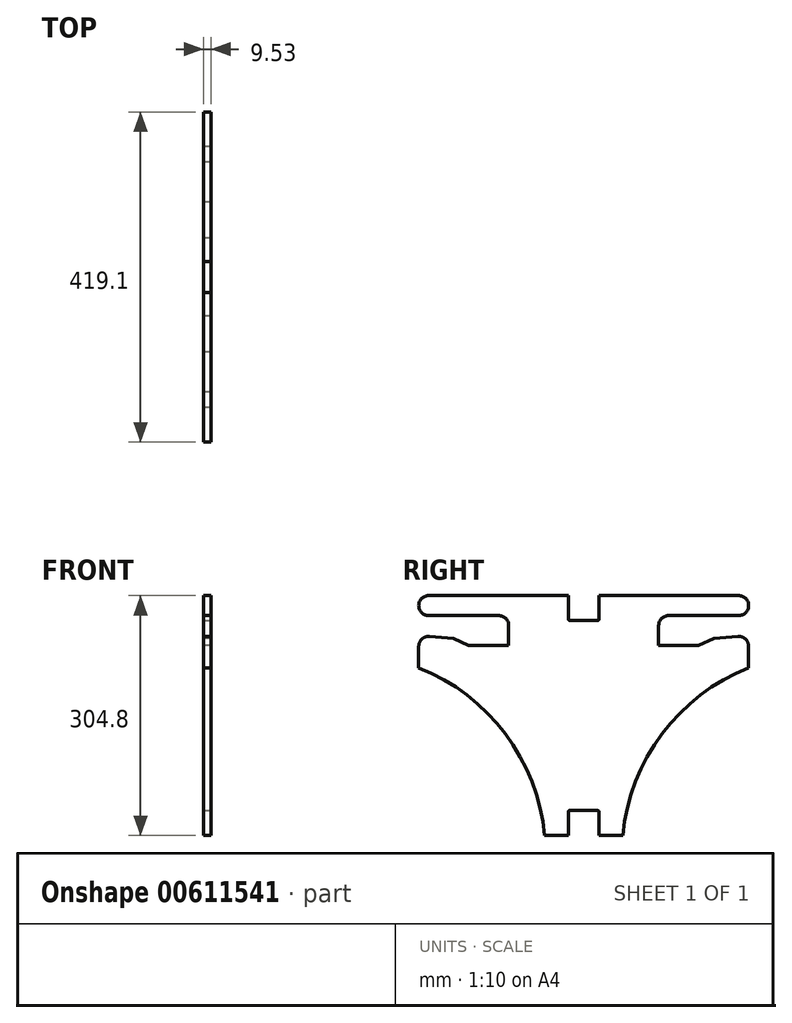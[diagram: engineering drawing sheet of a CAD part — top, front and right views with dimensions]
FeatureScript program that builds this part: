
annotation { "Feature Type Name" : "Feature", "Feature Type Description" : "" }
export const myFeature = defineFeature(function(context is Context, id is Id, definition is map)
    precondition{}
    {
        {
            var Q0;
            Q0=qCreatedBy(makeId("Right.planeOp"),FACE);
            var sketch = newSketch(context, id + "F0", { "sketchPlane" : qUnion([Q0])});
            skLineSegment(sketch, "E0.top", {"start": v(0, -31.75) * mm, "end": v(29.85, -31.75) * mm});
            skLineSegment(sketch, "E0.right", {"start": v(31.75, 0) * mm, "end": v(31.75, -29.84) * mm});
            skLineSegment(sketch, "E1", {"start": v(31.75, 0) * mm, "end": v(209.55, 0) * mm});
            skLineSegment(sketch, "E2", {"start": v(222.25, -12.7) * mm, "end": v(222.25, -12.7) * mm});
            skLineSegment(sketch, "E3", {"start": v(209.55, -25.4) * mm, "end": v(120.65, -25.4) * mm});
            skLineSegment(sketch, "E4", {"start": v(107.95, -38.1) * mm, "end": v(107.95, -63.5) * mm});
            skLineSegment(sketch, "E5", {"start": v(107.95, -63.5) * mm, "end": v(158.75, -63.5) * mm});
            skLineSegment(sketch, "E6", {"start": v(222.25, -64.65) * mm, "end": v(222.25, -91.85) * mm});
            skLineSegment(sketch, "E7", {"start": v(208.45, -52) * mm, "end": v(178.38, -54.6) * mm});
            skLineSegment(sketch, "E8", {"start": v(178.38, -54.6) * mm, "end": v(158.75, -63.5) * mm});
            skPoint(sketch, "E9.visualSharp", {"position": v(222.25, -25.4) * mm});
            skArc(sketch, "E9.filletArc", {"start": v(209.55, -25.4) * mm, "mid": v(218.53, -21.68) * mm, "end": v(222.25, -12.7) * mm});
            skPoint(sketch, "E10.visualSharp", {"position": v(222.25, 0) * mm});
            skArc(sketch, "E10.filletArc", {"start": v(222.25, -12.7) * mm, "mid": v(218.53, -3.72) * mm, "end": v(209.55, 0) * mm});
            skPoint(sketch, "E11.visualSharp", {"position": v(107.95, -25.4) * mm});
            skArc(sketch, "E11.filletArc", {"start": v(120.65, -25.4) * mm, "mid": v(111.67, -29.12) * mm, "end": v(107.95, -38.1) * mm});
            skPoint(sketch, "E12.visualSharp", {"position": v(222.25, -50.8) * mm});
            skArc(sketch, "E12.filletArc", {"start": v(222.25, -64.65) * mm, "mid": v(218.13, -55.3) * mm, "end": v(208.45, -52) * mm});
            skLineSegment(sketch, "E13", {"start": v(0, -31.75) * mm, "end": v(0, -273.05) * mm});
            skLineSegment(sketch, "E14", {"start": v(0, -273.05) * mm, "end": v(29.85, -273.05) * mm});
            skLineSegment(sketch, "E15", {"start": v(31.75, -274.95) * mm, "end": v(31.75, -304.8) * mm});
            skLineSegment(sketch, "E16", {"start": v(31.75, -304.8) * mm, "end": v(62.46, -304.8) * mm});
            skArc(sketch, "E17", {"start": v(222.25, -91.85) * mm, "mid": v(112.22, -175.71) * mm, "end": v(62.46, -304.8) * mm});
            skPoint(sketch, "E18.visualSharp", {"position": v(31.75, -31.75) * mm});
            skArc(sketch, "E18.filletArc", {"start": v(29.85, -31.75) * mm, "mid": v(31.2, -31.2) * mm, "end": v(31.75, -29.84) * mm});
            skPoint(sketch, "E19.visualSharp", {"position": v(31.75, -273.05) * mm});
            skArc(sketch, "E19.filletArc", {"start": v(31.75, -274.95) * mm, "mid": v(31.2, -273.6) * mm, "end": v(29.85, -273.05) * mm});
            skSolve(sketch);
        }
        {
            var Q0;
            Q0 = qSketchRegion(id + "F0", true);
            extrude(context, id + "F1", {"entities" : qUnion([Q0]), "depth" : 9.52 * mm, "offsetDistance" : 25.4 * mm});
        }
        {
            var Q0;
            Q0=makeQuery(id+"F1.opExtrude","CAP_FACE",FACE,{"disambiguationData":[OSD([sQuery(id+"F0.wireOp",EDGE,"E0.top"),sQuery(id+"F0.wireOp",EDGE,"E0.right"),sQuery(id+"F0.wireOp",EDGE,"E1"),sQuery(id+"F0.wireOp",EDGE,"E3"),sQuery(id+"F0.wireOp",EDGE,"E4"),sQuery(id+"F0.wireOp",EDGE,"E5"),sQuery(id+"F0.wireOp",EDGE,"E6"),sQuery(id+"F0.wireOp",EDGE,"E7"),sQuery(id+"F0.wireOp",EDGE,"E8"),sQuery(id+"F0.wireOp",EDGE,"E9.filletArc"),sQuery(id+"F0.wireOp",EDGE,"E10.filletArc"),sQuery(id+"F0.wireOp",EDGE,"E11.filletArc"),sQuery(id+"F0.wireOp",EDGE,"E12.filletArc"),sQuery(id+"F0.wireOp",EDGE,"E13"),sQuery(id+"F0.wireOp",EDGE,"E14"),sQuery(id+"F0.wireOp",EDGE,"E15"),sQuery(id+"F0.wireOp",EDGE,"E16"),sQuery(id+"F0.wireOp",EDGE,"E17"),sQuery(id+"F0.wireOp",EDGE,"E18.filletArc"),sQuery(id+"F0.wireOp",EDGE,"E19.filletArc")])],"isStart":false});
            var sketch = newSketch(context, id + "F2", { "sketchPlane" : qUnion([Q0])});
            skLineSegment(sketch, "E20.bottom", {"start": v(0, -31.75) * mm, "end": v(12.7, -31.75) * mm});
            skLineSegment(sketch, "E20.top", {"start": v(0, -273.05) * mm, "end": v(12.7, -273.05) * mm});
            skLineSegment(sketch, "E20.left", {"start": v(0, -31.75) * mm, "end": v(0, -273.05) * mm});
            skLineSegment(sketch, "E20.right", {"start": v(12.7, -31.75) * mm, "end": v(12.7, -273.05) * mm});
            skSolve(sketch);
        }
        {
            var Q0;
            Q0 = qSketchRegion(id + "F2", true);
            extrude(context, id + "F3", {"entities" : qUnion([Q0]), "operationType" : NewBodyOperationType.REMOVE, "oppositeDirection" : true, "depth" : 25.4 * mm, "offsetDistance" : 25.4 * mm});
        }
        {
            var Q0;
            Q0=makeQuery(id+"F1.opExtrude","SWEPT_BODY",BODY,{"disambiguationData":[OSD([sQuery(id+"F0.wireOp",EDGE,"E0.top"),sQuery(id+"F0.wireOp",EDGE,"E0.right"),sQuery(id+"F0.wireOp",EDGE,"E1"),sQuery(id+"F0.wireOp",EDGE,"E3"),sQuery(id+"F0.wireOp",EDGE,"E4"),sQuery(id+"F0.wireOp",EDGE,"E5"),sQuery(id+"F0.wireOp",EDGE,"E6"),sQuery(id+"F0.wireOp",EDGE,"E7"),sQuery(id+"F0.wireOp",EDGE,"E8"),sQuery(id+"F0.wireOp",EDGE,"E9.filletArc"),sQuery(id+"F0.wireOp",EDGE,"E10.filletArc"),sQuery(id+"F0.wireOp",EDGE,"E11.filletArc"),sQuery(id+"F0.wireOp",EDGE,"E12.filletArc"),sQuery(id+"F0.wireOp",EDGE,"E13"),sQuery(id+"F0.wireOp",EDGE,"E14"),sQuery(id+"F0.wireOp",EDGE,"E15"),sQuery(id+"F0.wireOp",EDGE,"E16"),sQuery(id+"F0.wireOp",EDGE,"E17"),sQuery(id+"F0.wireOp",EDGE,"E18.filletArc"),sQuery(id+"F0.wireOp",EDGE,"E19.filletArc")])]});
            var Q1;
            Q1=makeQuery(id+"F3.boolean.opBoolean","COPY",FACE,{"derivedFrom":makeQuery(id+"F3.opExtrude","SWEPT_FACE",FACE,{"disambiguationData":[OSD([sQuery(id+"F2.wireOp",EDGE,"E20.right")])]})});
            mirror(context, id + "F4", {"operationType" : NewBodyOperationType.ADD, "entities" : qUnion([Q0]), "mirrorPlane" : qUnion([Q1])});
        }
        {
            var Q0;
            {var subQ0=makeQuery(id+"F1.opExtrude","CAP_FACE",FACE,{"disambiguationData":[OSD([sQuery(id+"F0.wireOp",EDGE,"E0.top"),sQuery(id+"F0.wireOp",EDGE,"E0.right"),sQuery(id+"F0.wireOp",EDGE,"E1"),sQuery(id+"F0.wireOp",EDGE,"E3"),sQuery(id+"F0.wireOp",EDGE,"E4"),sQuery(id+"F0.wireOp",EDGE,"E5"),sQuery(id+"F0.wireOp",EDGE,"E6"),sQuery(id+"F0.wireOp",EDGE,"E7"),sQuery(id+"F0.wireOp",EDGE,"E8"),sQuery(id+"F0.wireOp",EDGE,"E9.filletArc"),sQuery(id+"F0.wireOp",EDGE,"E10.filletArc"),sQuery(id+"F0.wireOp",EDGE,"E11.filletArc"),sQuery(id+"F0.wireOp",EDGE,"E12.filletArc"),sQuery(id+"F0.wireOp",EDGE,"E13"),sQuery(id+"F0.wireOp",EDGE,"E14"),sQuery(id+"F0.wireOp",EDGE,"E15"),sQuery(id+"F0.wireOp",EDGE,"E16"),sQuery(id+"F0.wireOp",EDGE,"E17"),sQuery(id+"F0.wireOp",EDGE,"E18.filletArc"),sQuery(id+"F0.wireOp",EDGE,"E19.filletArc")])],"isStart":false});Q0=makeQuery(id+"F4.boolean.opBoolean","MERGE",FACE,{"derivedFrom":[subQ0,makeQuery(id+"F4.opPattern","COPY",FACE,{"derivedFrom":subQ0,"instanceName":"1"})]});}
            var sketch = newSketch(context, id + "F5", { "sketchPlane" : qUnion([Q0])});
            skLineSegment(sketch, "E21.bottom", {"start": v(-6.75, 0) * mm, "end": v(32.15, 0) * mm});
            skLineSegment(sketch, "E21.top", {"start": v(-4.84, -31.75) * mm, "end": v(30.24, -31.75) * mm});
            skLineSegment(sketch, "E21.left", {"start": v(-6.75, 0) * mm, "end": v(-6.75, -29.85) * mm});
            skLineSegment(sketch, "E21.right", {"start": v(32.15, 0) * mm, "end": v(32.15, -29.84) * mm});
            skPoint(sketch, "E22.visualSharp", {"position": v(-6.75, -31.75) * mm});
            skArc(sketch, "E22.filletArc", {"start": v(-6.75, -29.85) * mm, "mid": v(-6.19, -31.2) * mm, "end": v(-4.84, -31.75) * mm});
            skPoint(sketch, "E23.visualSharp", {"position": v(32.15, -31.75) * mm});
            skArc(sketch, "E23.filletArc", {"start": v(30.24, -31.75) * mm, "mid": v(31.59, -31.2) * mm, "end": v(32.15, -29.84) * mm});
            skLineSegment(sketch, "E24.bottom", {"start": v(-6.75, -304.8) * mm, "end": v(32.15, -304.8) * mm});
            skLineSegment(sketch, "E24.top", {"start": v(-4.84, -273.05) * mm, "end": v(30.24, -273.05) * mm});
            skLineSegment(sketch, "E24.left", {"start": v(-6.75, -304.8) * mm, "end": v(-6.75, -274.95) * mm});
            skLineSegment(sketch, "E24.right", {"start": v(32.15, -304.8) * mm, "end": v(32.15, -274.95) * mm});
            skPoint(sketch, "E25.visualSharp", {"position": v(-6.75, -273.05) * mm});
            skArc(sketch, "E25.filletArc", {"start": v(-4.84, -273.05) * mm, "mid": v(-6.19, -273.6) * mm, "end": v(-6.75, -274.95) * mm});
            skPoint(sketch, "E26.visualSharp", {"position": v(32.15, -273.05) * mm});
            skArc(sketch, "E26.filletArc", {"start": v(32.15, -274.95) * mm, "mid": v(31.59, -273.6) * mm, "end": v(30.24, -273.05) * mm});
            skSolve(sketch);
        }
        {
            var Q0;
            Q0 = qSketchRegion(id + "F5", true);
            extrude(context, id + "F6", {"entities" : qUnion([Q0]), "operationType" : NewBodyOperationType.REMOVE, "oppositeDirection" : true, "depth" : 25.4 * mm, "offsetDistance" : 25.4 * mm});
        }
    });
